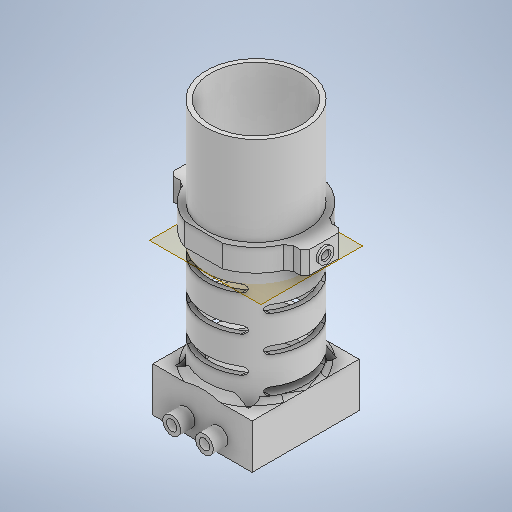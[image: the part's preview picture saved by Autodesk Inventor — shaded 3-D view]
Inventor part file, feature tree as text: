
AUTODESK INVENTOR PART (.ipt)
format: ipt  version: 2025 (Build 290162010, 162A)  size: 706,048 bytes
history: native  units: in
note: dims shown in document units (in); Inventor stores cm internally (conversion verified against a paired STEP export)
features: extrude x13, sketch x13, plane x4, chamfer x3, fillet x2, other x1
ambient origin geometry x8: Origin, YZ Plane, XZ Plane, XY Plane, X Axis, Y Axis, Z Axis, Center Point
bodies: Volumenkörper1 (feature_tree)
feature tree (36):
  extrude  "Extrusion1"  Depth=1.2598in
  extrude  "Extrusion2"  Depth=1.5551in
  extrude  "Extrusion4"  Depth=0.7874in TaperAngle=0.0deg
  other  "Verdickung1"
  fillet  "Rundung4"  Radius=0.0787in
  chamfer  "Fasen4"  Distance=3.937in
  extrude  "Extrusion9"  Depth=0.0787in
  extrude  "Extrusion10"  Depth=0.0787in
  extrude  "Extrusion11"  Depth=0.2559in TaperAngle=0.0deg
  plane  "Arbeitsebene1"
  extrude  "Extrusion12"  Depth=0.5787in
  plane  "Arbeitsebene2"
  extrude  "Extrusion13"  Depth=0.2559in TaperAngle=0.0deg
  plane  "Arbeitsebene3"
  extrude  "Extrusion14"  TaperAngle=0.0deg  [1 undecoded]
  fillet  "Rundung5"  Radius=0.1378in
  extrude  "Extrusion16"  TaperAngle=0.0deg  [1 undecoded]
  plane  "Arbeitsebene4"
  extrude  "Extrusion17"  Depth=0.4921in
  extrude  "Extrusion18"  Depth=0.1378in
  extrude  "Extrusion19"  Depth=0.3937in
  chamfer  "Fasen5"  Distance=0.4921in
  chamfer  "Fasen6"  [1 undecoded]
  sketch  "Skizze1"  dims[d0=1.752in d1=1.2598in]
  sketch  "Skizze2"  dims[d2=0.0787in d3=0.0in d4=1.5551in]
  sketch  "Skizze4"  dims[d5=1.2992in d7=0.7874in d8=0.0in d15=0.0787in d16=3.937in d17=0.0in]
  sketch  "Skizze10"  dims[d40=0.0787in d41=0.0787in]
  sketch  "Skizze11"  dims[d47=1.8898in d53=0.0787in]
  sketch  "Skizze12"  dims[d54=0.1181in d55=0.0787in d56=45.0deg d57=0.2559in d58=0.0in]
  sketch  "Skizze13"  dims[d59=0.5217in d60=0.5787in]
  sketch  "Skizze14"  dims[d61=0.315in d62=0.2559in d63=0.0in]
  sketch  "Skizze15"  dims[d64=0.187in d65=0.0in d66=0.0in d67=0.1378in]
  sketch  "Skizze17"  dims[d68=0.0787in d71=0.0in d72=0.0in]
  sketch  "Skizze18"  dims[d73=0.4921in d74=0.4921in]
  sketch  "Skizze19"  dims[d75=1.1024in d76=0.1378in]
  sketch  "Skizze20"  dims[d77=0.3937in d78=1.1024in d80=0.4921in d81=0.0in d82=0.0in d83=0.4921in d84=-1.9685in d85=0.9843in d86=0.3937in d87=0.0in d89=0.0591in d90=0.0in d91=0.0787in d92=0.9252in d93=0.2756in d99=0.1319in d102=0.3937in d103=0.0in d104=1.7323in d105=0.0787in d106=0.0in d107=0.2756in d108=0.0394in d109=0.0in d110=0.2756in d111=0.0394in d112=0.0in d113=0.0787in d114=0.0787in d115=45.0deg d116=0.0197in d117=0.0787in d118=45.0deg]
note: 3 required parameter values undecoded (feature->parameter linkage not recoverable at this tier; creation-order binding heuristic only, values carry confidence <= 0.55)
